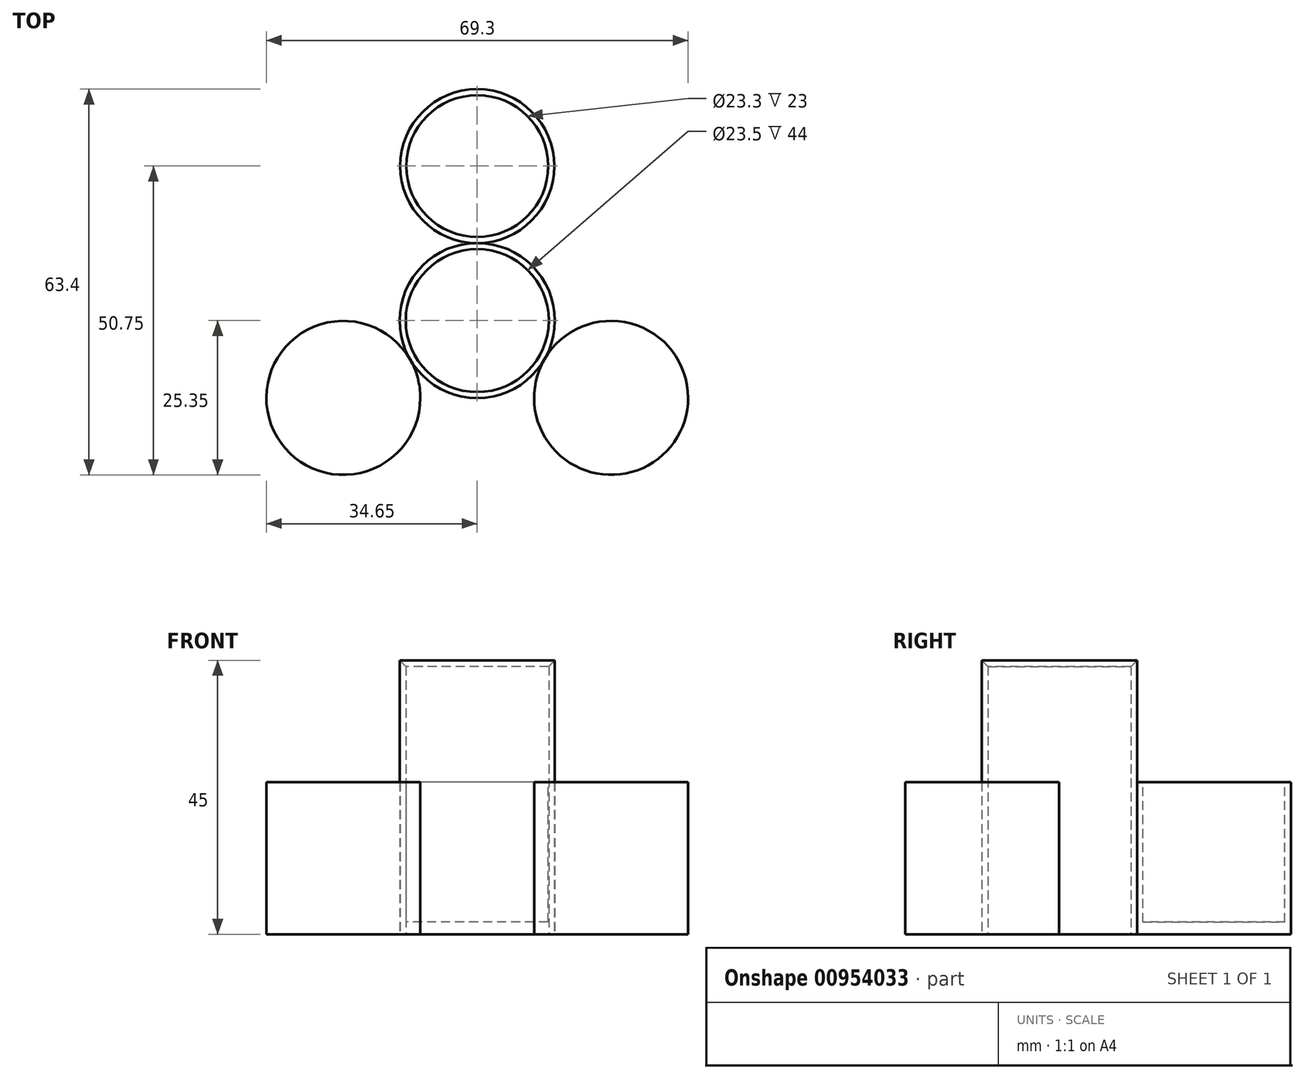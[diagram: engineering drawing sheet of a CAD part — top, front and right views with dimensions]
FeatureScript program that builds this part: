
annotation { "Feature Type Name" : "Feature", "Feature Type Description" : "" }
export const myFeature = defineFeature(function(context is Context, id is Id, definition is map)
    precondition{}
    {
        {
            var Q0;
            Q0=qCreatedBy(makeId("Top.planeOp"),FACE);
            var sketch = newSketch(context, id + "F0", { "sketchPlane" : qUnion([Q0])});
            skCircle(sketch, "E0", {"center": v(0, 0) * mm, "radius": 11.75 * mm});
            skCircle(sketch, "E1", {"center": v(0, 0) * mm, "radius": 12.75 * mm});
            skCircle(sketch, "E2", {"center": v(0, 25.4) * mm, "radius": 12.65 * mm});
            skCircle(sketch, "E3.1.1", {"center": v(-22, -12.7) * mm, "radius": 12.65 * mm});
            skCircle(sketch, "E3.2.1", {"center": v(22, -12.7) * mm, "radius": 12.65 * mm});
            skSolve(sketch);
        }
        {
            var Q0;
            Q0=makeQuery(id+"F0.imprint","IMPRINT",FACE,{"disambiguationData":[TD([[makeQuery(id+"F0.imprint","IMPRINT",EDGE,{"derivedFrom":sQuery(id+"F0.wireOp",EDGE,"E0")}),-1.0]])]});
            extrude(context, id + "F1", {"entities" : qUnion([Q0]), "depth" : 45 * mm, "offsetDistance" : 25 * mm});
        }
        {
            var Q0;
            Q0 = qSketchRegion(id + "F0", true);
            extrude(context, id + "F2", {"entities" : qUnion([Q0]), "operationType" : NewBodyOperationType.ADD, "depth" : 25 * mm, "offsetDistance" : 25 * mm});
        }
        {
            var Q0;
            Q0=makeQuery(id+"F2.opExtrude","CAP_EDGE",EDGE,{"disambiguationData":[OSD([sQuery(id+"F0.wireOp",EDGE,"E3.1.0")])],"isStart":false});
            var Q1;
            Q1=makeQuery(id+"F2.opExtrude","CAP_EDGE",EDGE,{"disambiguationData":[OSD([sQuery(id+"F0.wireOp",EDGE,"E3.2.0")])],"isStart":false});
            var Q2;
            Q2=makeQuery(id+"F2.opExtrude","CAP_EDGE",EDGE,{"disambiguationData":[OSD([sQuery(id+"F0.wireOp",EDGE,"tU6Cnpxp-ITqo-fKxo-Cbf7-EsG6j6J603GD")])],"isStart":false});
            var Q3;
            Q3=makeQuery(id+"F1.opExtrude","CAP_EDGE",EDGE,{"disambiguationData":[OSD([sQuery(id+"F0.wireOp",EDGE,"E0")])],"isStart":false});
            chamfer(context, id + "F3", {"entities" : qUnion([Q0, Q1, Q2, Q3]), "width" : 1 * mm, "tangentPropagation" : true});
        }
        {
            var Q0;
            Q0=makeQuery(id+"F2.opExtrude","CAP_FACE",FACE,{"disambiguationData":[OSD([sQuery(id+"F0.wireOp",EDGE,"E2")])],"isStart":false});
            var sketch = newSketch(context, id + "F4", { "sketchPlane" : qUnion([Q0])});
            skCircle(sketch, "E4", {"center": v(0, 25.4) * mm, "radius": 11.65 * mm});
            skCircle(sketch, "E5.1.0", {"center": v(-22, -12.7) * mm, "radius": 11.65 * mm});
            skCircle(sketch, "E5.2.0", {"center": v(22, -12.7) * mm, "radius": 11.65 * mm});
            skPoint(sketch, "E5.center", {"position": v(0, 0) * mm});
            skSolve(sketch);
        }
        {
            var Q0;
            Q0=makeQuery(id+"F4.imprint","IMPRINT",FACE,{"disambiguationData":[TD([[makeQuery(id+"F4.imprint","IMPRINT",EDGE,{"derivedFrom":sQuery(id+"F4.wireOp",EDGE,"E4")}),1.0]])]});
            extrude(context, id + "F5", {"entities" : qUnion([Q0]), "operationType" : NewBodyOperationType.REMOVE, "oppositeDirection" : true, "depth" : 23 * mm, "offsetDistance" : 25 * mm});
        }
    });
